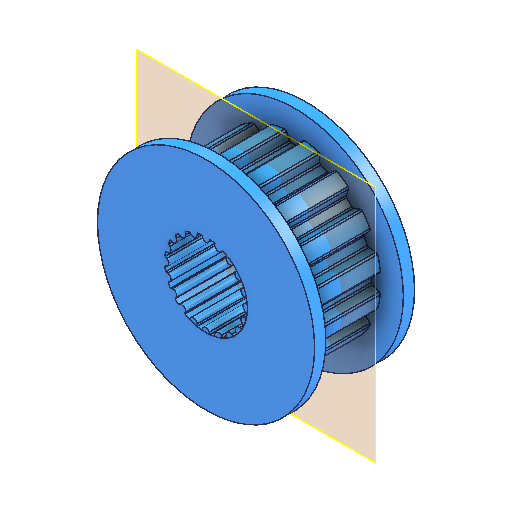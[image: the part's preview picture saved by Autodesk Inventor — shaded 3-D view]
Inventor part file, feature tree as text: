
AUTODESK INVENTOR PART (.ipt)
format: ipt  version: 2025.2 (Build 292293000, 293)  size: 776,192 bytes
history: native  units: in
note: dims shown in document units (in); Inventor stores cm internally (conversion verified against a paired STEP export)
features: sketch x5, extrude x4, plane x1
ambient origin geometry x8: Origin, YZ Plane, XZ Plane, XY Plane, X Axis, Y Axis, Z Axis, Center Point
bodies: Solid1 (feature_tree)
feature tree (10):
  extrude  "Extrusion1"  Depth=1.2402in
  plane  "Work Plane1"
  extrude  "Extrusion2"  [1 undecoded]
  extrude  "Extrusion3"  Depth=0.4429in TaperAngle=0.0deg
  extrude  "Extrusion5"  TaperAngle=0.0deg  [1 undecoded]
  sketch  "Sketch1"  dims[d0=0.4724in d1=1.2402in]
  sketch  "Sketch2"  dims[d5=0.9843in d6=0.4429in d7=0.0in]
  sketch  "Sketch3"  dims[d8=0.0in d9=0.0in]
  sketch  "Sketch Circular Pattern1"  dims[d2=0.5709in d3=0.0in d4=-0.2854in]
  sketch  "Sketch6"  dims[d12=0.5709in d13=0.0in d18=14.5669in d20=360.0deg d40=0.4429in d41=0.0in d45=0.9843in d46=0.0in d47=0.0in d48=0.0in d49=0.0in]
note: 2 required parameter values undecoded (feature->parameter linkage not recoverable at this tier; creation-order binding heuristic only, values carry confidence <= 0.55)
